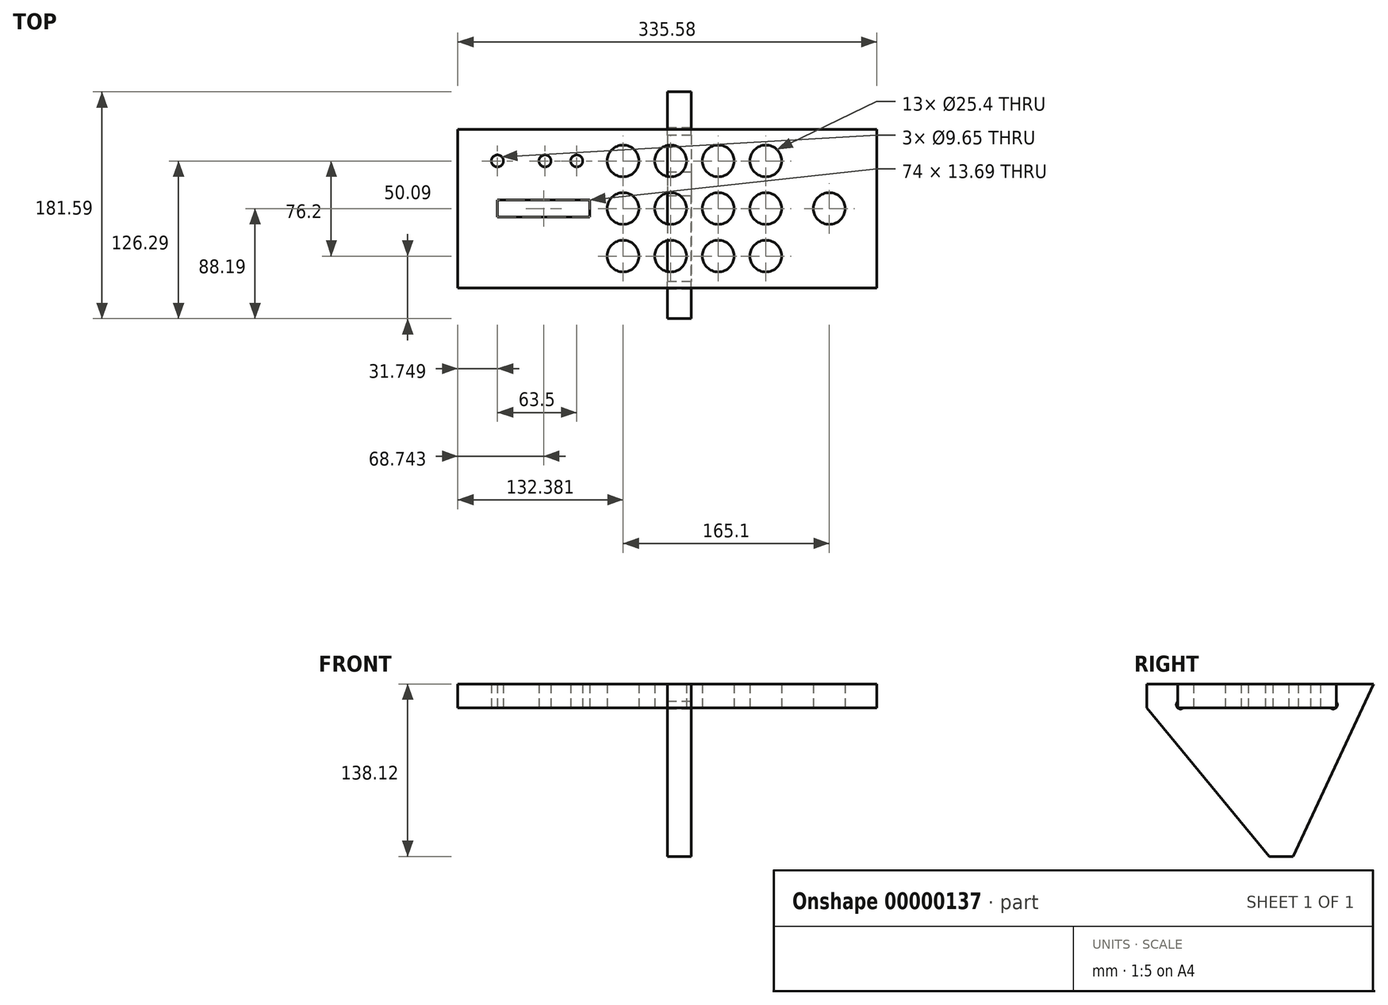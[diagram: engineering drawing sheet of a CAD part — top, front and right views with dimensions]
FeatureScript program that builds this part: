
annotation { "Feature Type Name" : "Feature", "Feature Type Description" : "" }
export const myFeature = defineFeature(function(context is Context, id is Id, definition is map)
    precondition{}
    {
        {
            var Q0;
            Q0=qCreatedBy(makeId("Top.planeOp"),FACE);
            var sketch = newSketch(context, id + "F0", { "sketchPlane" : qUnion([Q0])});
            skLineSegment(sketch, "E0.rect.bottom", {"start": v(-167.8, 63.5) * mm, "end": v(167.8, 63.5) * mm});
            skLineSegment(sketch, "E0.rect.top", {"start": v(-167.8, -63.5) * mm, "end": v(167.8, -63.5) * mm});
            skLineSegment(sketch, "E0.rect.left", {"start": v(-167.8, 63.5) * mm, "end": v(-167.8, -63.5) * mm});
            skLineSegment(sketch, "E0.rect.right", {"start": v(167.8, 63.5) * mm, "end": v(167.8, -63.5) * mm});
            skPoint(sketch, "E0.rect.middle", {"position": v(0, 0) * mm});
            skCircle(sketch, "E1", {"center": v(-35.4, 38.1) * mm, "radius": 12.7 * mm});
            skCircle(sketch, "E2", {"center": v(-35.4, 0) * mm, "radius": 12.7 * mm});
            skCircle(sketch, "E3", {"center": v(-35.4, -38.1) * mm, "radius": 12.7 * mm});
            skCircle(sketch, "E4", {"center": v(2.7, 38.1) * mm, "radius": 12.7 * mm});
            skCircle(sketch, "E5", {"center": v(2.7, 0) * mm, "radius": 12.7 * mm});
            skCircle(sketch, "E6", {"center": v(2.7, -38.1) * mm, "radius": 12.7 * mm});
            skCircle(sketch, "E7", {"center": v(40.8, -38.1) * mm, "radius": 12.7 * mm});
            skCircle(sketch, "E8", {"center": v(40.8, 0) * mm, "radius": 12.7 * mm});
            skCircle(sketch, "E9", {"center": v(40.8, 38.1) * mm, "radius": 12.7 * mm});
            skCircle(sketch, "E10", {"center": v(78.9, 38.1) * mm, "radius": 12.7 * mm});
            skCircle(sketch, "E11", {"center": v(78.9, 0) * mm, "radius": 12.7 * mm});
            skCircle(sketch, "E12", {"center": v(78.9, -38.1) * mm, "radius": 12.7 * mm});
            skCircle(sketch, "E13", {"center": v(-136.04, 38.1) * mm, "radius": 4.83 * mm});
            skCircle(sketch, "E14", {"center": v(-97.94, 38.1) * mm, "radius": 4.83 * mm});
            skCircle(sketch, "E15", {"center": v(-72.54, 38.1) * mm, "radius": 4.83 * mm});
            skLineSegment(sketch, "E16", {"start": v(-72.54, 38.1) * mm, "end": v(-35.4, 38.1) * mm, "construction": true});
            skCircle(sketch, "E17", {"center": v(129.7, 0) * mm, "radius": 12.7 * mm});
            skLineSegment(sketch, "E18", {"start": v(148.74, 63.5) * mm, "end": v(148.74, -63.5) * mm, "construction": true});
            skLineSegment(sketch, "E19", {"start": v(-148.74, 63.5) * mm, "end": v(-148.74, -63.5) * mm, "construction": true});
            skLineSegment(sketch, "E20", {"start": v(-148.74, -63.5) * mm, "end": v(-169, -63.24) * mm, "construction": true});
            skLineSegment(sketch, "E21", {"start": v(-9.52, 63.5) * mm, "end": v(-9.53, -63.5) * mm, "construction": true});
            skLineSegment(sketch, "E22", {"start": v(0, 0) * mm, "end": v(0, 63.5) * mm, "construction": true});
            skLineSegment(sketch, "E23.0.MirrorCS", {"start": v(9.53, 63.5) * mm, "end": v(9.52, -63.5) * mm, "construction": true});
            skLineSegment(sketch, "E24.rect.bottom", {"start": v(-62.05, -6.84) * mm, "end": v(-136.05, -6.84) * mm});
            skLineSegment(sketch, "E24.rect.top", {"start": v(-62.05, 6.84) * mm, "end": v(-136.05, 6.84) * mm});
            skLineSegment(sketch, "E24.rect.left", {"start": v(-62.05, -6.84) * mm, "end": v(-62.05, 6.84) * mm});
            skLineSegment(sketch, "E24.rect.right", {"start": v(-136.05, -6.84) * mm, "end": v(-136.05, 6.84) * mm});
            skPoint(sketch, "E24.rect.middle", {"position": v(-99.05, 0) * mm});
            skLineSegment(sketch, "E25", {"start": v(-99.05, 0) * mm, "end": v(-99.05, 63.5) * mm, "construction": true});
            skSolve(sketch);
        }
        {
            var Q0;
            Q0=makeQuery(id+"F0.imprint","IMPRINT",FACE,{"disambiguationData":[TD([[makeQuery(id+"F0.imprint","IMPRINT",EDGE,{"derivedFrom":sQuery(id+"F0.wireOp",EDGE,"E0.rect.bottom")}),-1.0]])]});
            extrude(context, id + "F1", {"entities" : qUnion([Q0]), "depth" : 19.05 * mm});
        }
        {
            var Q0;
            Q0=qCreatedBy(makeId("Right.planeOp"),FACE);
            var sketch = newSketch(context, id + "F2", { "sketchPlane" : qUnion([Q0])});
            skLineSegment(sketch, "E26.0", {"start": v(63.5, 0) * mm, "end": v(-63.5, 0) * mm});
            skLineSegment(sketch, "E26.1", {"start": v(63.5, 19.05) * mm, "end": v(63.5, 0) * mm});
            skLineSegment(sketch, "E26.2", {"start": v(-63.5, 19.05) * mm, "end": v(-63.5, 0) * mm});
            skLineSegment(sketch, "E27", {"start": v(63.5, 19.05) * mm, "end": v(93.4, 19.05) * mm});
            skLineSegment(sketch, "E28", {"start": v(93.4, 19.05) * mm, "end": v(29, -119.07) * mm});
            skLineSegment(sketch, "E29", {"start": v(29, -119.07) * mm, "end": v(9.95, -119.07) * mm});
            skLineSegment(sketch, "E30", {"start": v(-88.19, 19.05) * mm, "end": v(-63.5, 19.05) * mm});
            skLineSegment(sketch, "E31", {"start": v(-88.19, 19.05) * mm, "end": v(-88.19, 0) * mm});
            skLineSegment(sketch, "E32", {"start": v(-88.19, 0) * mm, "end": v(9.95, -119.07) * mm});
            skLineSegment(sketch, "E33", {"start": v(-63.5, 0) * mm, "end": v(-78.2, -12.12) * mm, "construction": true});
            skLineSegment(sketch, "E34", {"start": v(63.5, 0) * mm, "end": v(80.77, -8.05) * mm, "construction": true});
            skArc(sketch, "E35", {"start": v(58.56, 0) * mm, "mid": v(63.5, 0) * mm, "end": v(63.5, 4.94) * mm});
            skLineSegment(sketch, "E36", {"start": v(0, 0) * mm, "end": v(0, 19.17) * mm, "construction": true});
            skArc(sketch, "E37.0.MirrorCS", {"start": v(-58.56, 0) * mm, "mid": v(-63.5, 0) * mm, "end": v(-63.5, 4.94) * mm});
            skSolve(sketch);
        }
        {
            var Q0;
            {var subQ12=sQuery(id+"F2.wireOp",EDGE,"E27");Q0=makeQuery(id+"F2.imprint","IMPRINT",FACE,{"disambiguationData":[TD([[makeQuery(id+"F2.imprint","IMPRINT",EDGE,{"derivedFrom":subQ12}),-1.0]])]});}
            extrude(context, id + "F3", {"entities" : qUnion([Q0]), "depth" : 19.05 * mm});
        }
    });
